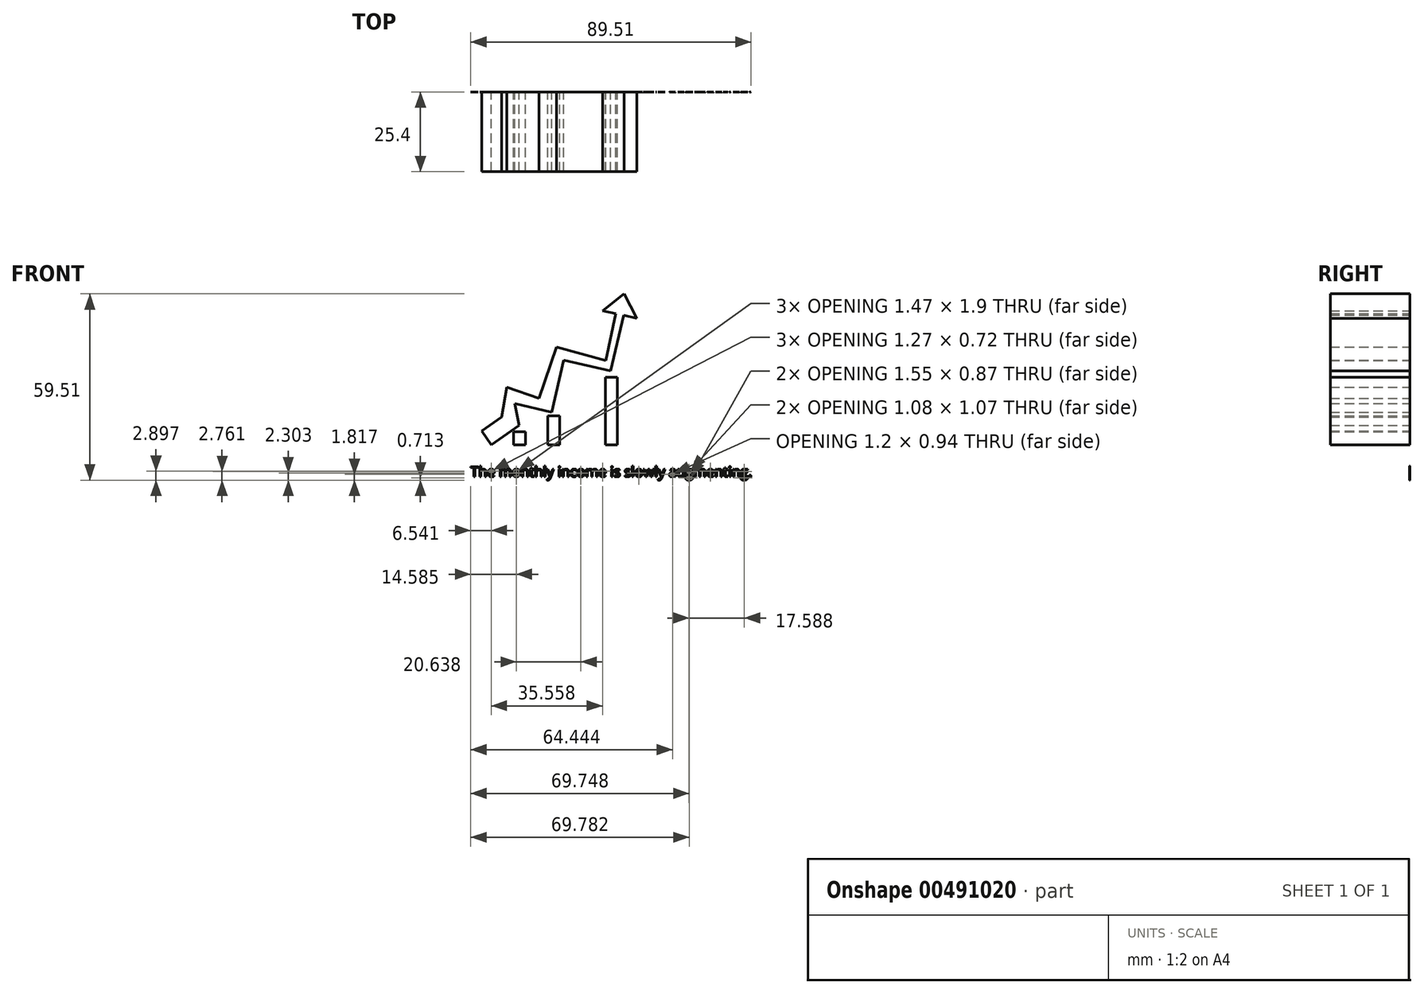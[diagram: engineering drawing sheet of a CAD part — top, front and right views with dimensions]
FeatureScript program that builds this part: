
annotation { "Feature Type Name" : "Feature", "Feature Type Description" : "" }
export const myFeature = defineFeature(function(context is Context, id is Id, definition is map)
    precondition{}
    {
        {
            var Q0;
            Q0=qCreatedBy(makeId("Front.planeOp"),FACE);
            var sketch = newSketch(context, id + "F0", { "sketchPlane" : qUnion([Q0])});
            skLineSegment(sketch, "E0", {"start": v(0, 0) * mm, "end": v(-3.13, 4.42) * mm});
            skLineSegment(sketch, "E1", {"start": v(-3.13, 4.42) * mm, "end": v(3.24, 8.94) * mm});
            skLineSegment(sketch, "E2", {"start": v(3.24, 8.94) * mm, "end": v(4.96, 18.46) * mm});
            skLineSegment(sketch, "E3", {"start": v(4.96, 18.46) * mm, "end": v(15.16, 14.91) * mm});
            skLineSegment(sketch, "E4", {"start": v(15.16, 14.91) * mm, "end": v(20.84, 31.21) * mm});
            skLineSegment(sketch, "E5", {"start": v(20.84, 31.21) * mm, "end": v(36.5, 26.9) * mm});
            skLineSegment(sketch, "E6", {"start": v(36.5, 26.9) * mm, "end": v(39.76, 41.9) * mm});
            skLineSegment(sketch, "E7", {"start": v(39.76, 41.9) * mm, "end": v(35.47, 42.83) * mm});
            skLineSegment(sketch, "E8", {"start": v(0, 0) * mm, "end": v(8.82, 6.25) * mm});
            skLineSegment(sketch, "E9", {"start": v(8.82, 6.25) * mm, "end": v(7.43, 13.22) * mm});
            skLineSegment(sketch, "E10", {"start": v(7.43, 13.22) * mm, "end": v(19.3, 10.48) * mm});
            skLineSegment(sketch, "E11", {"start": v(19.3, 10.48) * mm, "end": v(23.12, 27.06) * mm});
            skLineSegment(sketch, "E12", {"start": v(23.12, 27.06) * mm, "end": v(38.1, 23.6) * mm});
            skLineSegment(sketch, "E13", {"start": v(38.1, 23.6) * mm, "end": v(42.21, 41.38) * mm});
            skLineSegment(sketch, "E14", {"start": v(42.21, 41.38) * mm, "end": v(46.5, 40.4) * mm});
            skLineSegment(sketch, "E15", {"start": v(39.76, 41.9) * mm, "end": v(42.21, 41.38) * mm});
            skLineSegment(sketch, "E16", {"start": v(40.99, 41.64) * mm, "end": v(42.38, 48.25) * mm});
            skLineSegment(sketch, "E17", {"start": v(42.38, 48.25) * mm, "end": v(35.47, 42.83) * mm});
            skLineSegment(sketch, "E18", {"start": v(42.38, 48.25) * mm, "end": v(46.5, 40.4) * mm});
            skLineSegment(sketch, "E19", {"start": v(-8.3, 0) * mm, "end": v(63.5, 0) * mm});
            skLineSegment(sketch, "E20", {"start": v(63.5, 0) * mm, "end": v(63.5, 58.55) * mm});
            skLineSegment(sketch, "E21", {"start": v(63.5, 58.55) * mm, "end": v(-8.3, 58.55) * mm});
            skLineSegment(sketch, "E22", {"start": v(-8.3, 58.55) * mm, "end": v(-8.3, 0) * mm});
            skLineSegment(sketch, "E23", {"start": v(7.05, 0) * mm, "end": v(7.05, 4.18) * mm});
            skLineSegment(sketch, "E24", {"start": v(7.05, 4.18) * mm, "end": v(10.89, 4.18) * mm});
            skLineSegment(sketch, "E25", {"start": v(10.89, 4.18) * mm, "end": v(10.89, 0) * mm});
            skLineSegment(sketch, "E26", {"start": v(18.01, 9.33) * mm, "end": v(21.85, 9.33) * mm});
            skLineSegment(sketch, "E27", {"start": v(18.01, 9.33) * mm, "end": v(18.01, 0) * mm});
            skLineSegment(sketch, "E28", {"start": v(21.85, 9.33) * mm, "end": v(21.85, 0) * mm});
            skLineSegment(sketch, "E29", {"start": v(36.43, 21.6) * mm, "end": v(40.27, 21.6) * mm});
            skLineSegment(sketch, "E30", {"start": v(36.43, 21.6) * mm, "end": v(36.43, 0) * mm});
            skLineSegment(sketch, "E31", {"start": v(40.27, 21.6) * mm, "end": v(40.27, 0) * mm});
            skSolve(sketch);
        }
        {
            var Q0;
            Q0=makeQuery(id+"F0.imprint","IMPRINT",FACE,{"disambiguationData":[TD([[makeQuery(id+"F0.imprint","IMPRINT",EDGE,{"derivedFrom":sQuery(id+"F0.wireOp",EDGE,"E0")}),-1.0]])]});
            var Q1;
            Q1=makeQuery(id+"F0.imprint","IMPRINT",FACE,{"disambiguationData":[TD([[makeQuery(id+"F0.imprint","IMPRINT",EDGE,{"derivedFrom":sQuery(id+"F0.wireOp",EDGE,"E26")}),-1.0]])]});
            var Q2;
            {var subQ0=sQuery(id+"F0.wireOp",EDGE,"E23");Q2=makeQuery(id+"F0.imprint","IMPRINT",FACE,{"disambiguationData":[TD([[makeQuery(id+"F0.imprint","IMPRINT",EDGE,{"derivedFrom":subQ0}),-1.0]])]});}
            var Q3;
            Q3=makeQuery(id+"F0.imprint","IMPRINT",FACE,{"disambiguationData":[TD([[makeQuery(id+"F0.imprint","IMPRINT",EDGE,{"derivedFrom":sQuery(id+"F0.wireOp",EDGE,"E29")}),-1.0]])]});
            var Q4;
            {var subQ0=sQuery(id+"F0.wireOp",EDGE,"E7");Q4=makeQuery(id+"F0.imprint","IMPRINT",FACE,{"disambiguationData":[TD([[makeQuery(id+"F0.imprint","IMPRINT",EDGE,{"derivedFrom":subQ0}),-1.0]])]});}
            var Q5;
            {var subQ0=sQuery(id+"F0.wireOp",EDGE,"E14");Q5=makeQuery(id+"F0.imprint","IMPRINT",FACE,{"disambiguationData":[TD([[makeQuery(id+"F0.imprint","IMPRINT",EDGE,{"derivedFrom":subQ0}),1.0]])]});}
            extrude(context, id + "F1", {"entities" : qUnion([Q0, Q1, Q2, Q3, Q4, Q5]), "depth" : 25.4 * mm});
        }
        {
            var Q0;
            Q0=qCreatedBy(makeId("Front.planeOp"),FACE);
            var sketch = newSketch(context, id + "F2", { "sketchPlane" : qUnion([Q0])});
            skText(sketch, "E32", { "text": "The monthly income is slowly augmenting.\n", "fontName": "OpenSans-Regular.ttf"});
            const initialGuessF2  = {"E32": [-0.00667, -0.01017, 1, 0, 0.00327]};
            skSetInitialGuess(sketch, initialGuessF2);
            skSolve(sketch);
        }
        {
            var Q0;
            Q0 = qSketchRegion(id + "F2", true);
            extrude(context, id + "F3", {"entities" : qUnion([Q0]), "depth" : 0.05 * mm});
        }
    });
